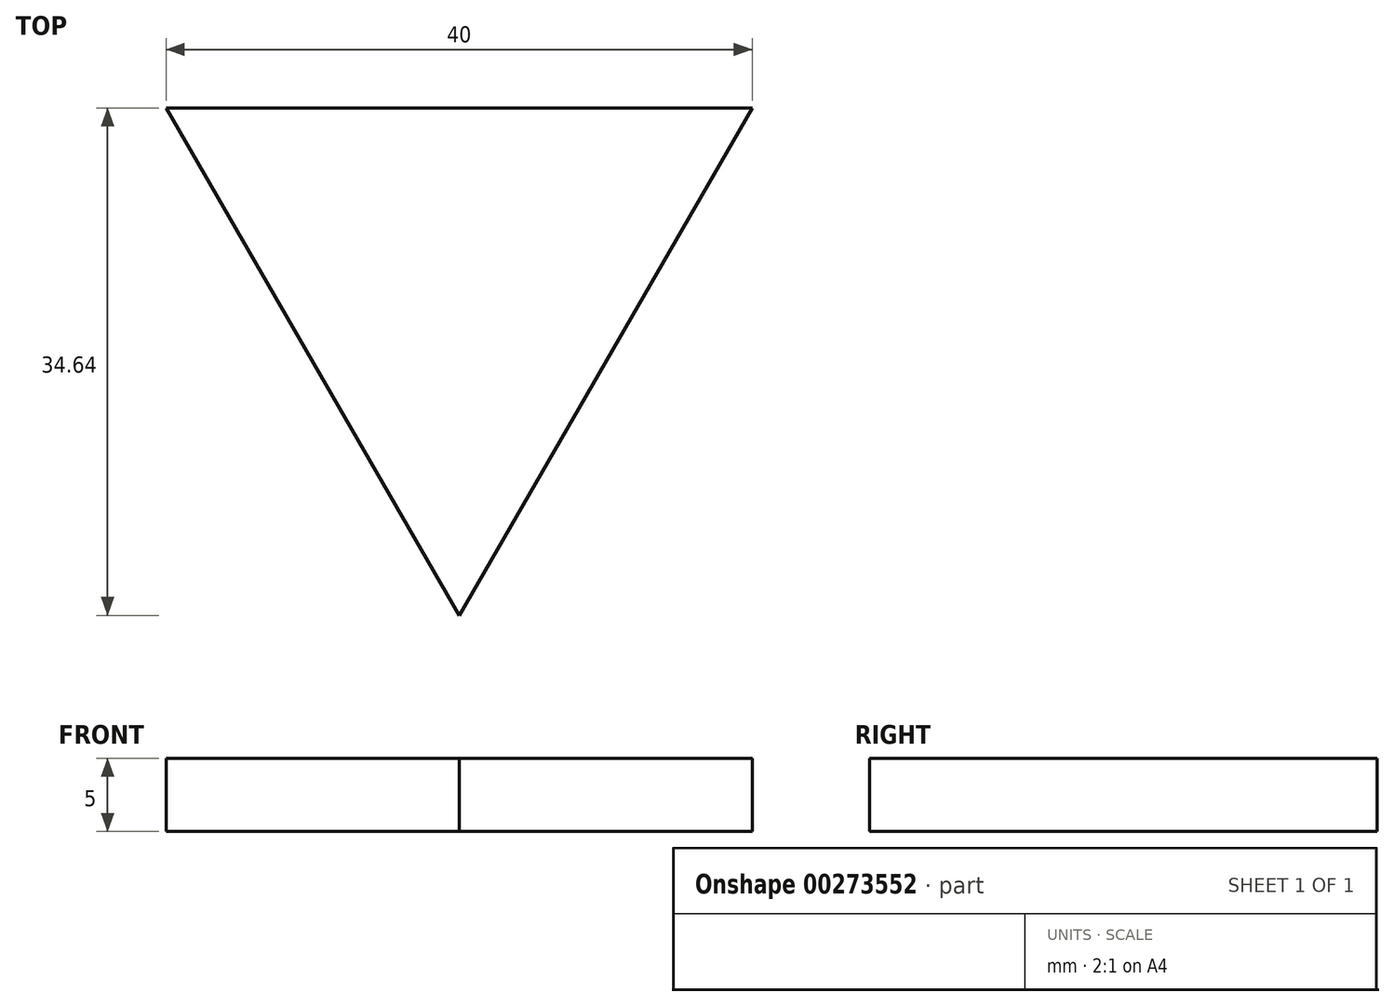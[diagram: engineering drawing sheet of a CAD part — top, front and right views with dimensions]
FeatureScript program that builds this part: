
annotation { "Feature Type Name" : "Feature", "Feature Type Description" : "" }
export const myFeature = defineFeature(function(context is Context, id is Id, definition is map)
    precondition{}
    {
        {
            var Q0;
            Q0=qCreatedBy(makeId("Top.planeOp"),FACE);
            var sketch = newSketch(context, id + "F0", { "sketchPlane" : qUnion([Q0])});
            skLineSegment(sketch, "E0", {"start": v(0, 0) * mm, "end": v(20, 34.64) * mm});
            skLineSegment(sketch, "E1", {"start": v(20, 34.64) * mm, "end": v(-20, 34.64) * mm});
            skLineSegment(sketch, "E2", {"start": v(-20, 34.64) * mm, "end": v(0, 0) * mm});
            skSolve(sketch);
        }
        {
            var Q0;
            Q0=makeQuery(id+"F0.imprint","IMPRINT",FACE,{"disambiguationData":[TD([[makeQuery(id+"F0.imprint","IMPRINT",EDGE,{"derivedFrom":sQuery(id+"F0.wireOp",EDGE,"E0")}),1.0]])]});
            extrude(context, id + "F1", {"entities" : qUnion([Q0]), "depth" : 5 * mm});
        }
        {
            var Q0;
            Q0=makeQuery(id+"F1.opExtrude","CAP_FACE",FACE,{"disambiguationData":[OSD([sQuery(id+"F0.wireOp",EDGE,"E0"),sQuery(id+"F0.wireOp",EDGE,"E1"),sQuery(id+"F0.wireOp",EDGE,"E2")])],"isStart":false});
            cPlane(context, id + "F2", {"entities" : qUnion([Q0]), "cplaneType" : CPlaneType.OFFSET, "offset" : 40 * mm, "width" : 150 * mm, "height" : 150 * mm});
        }
    });
